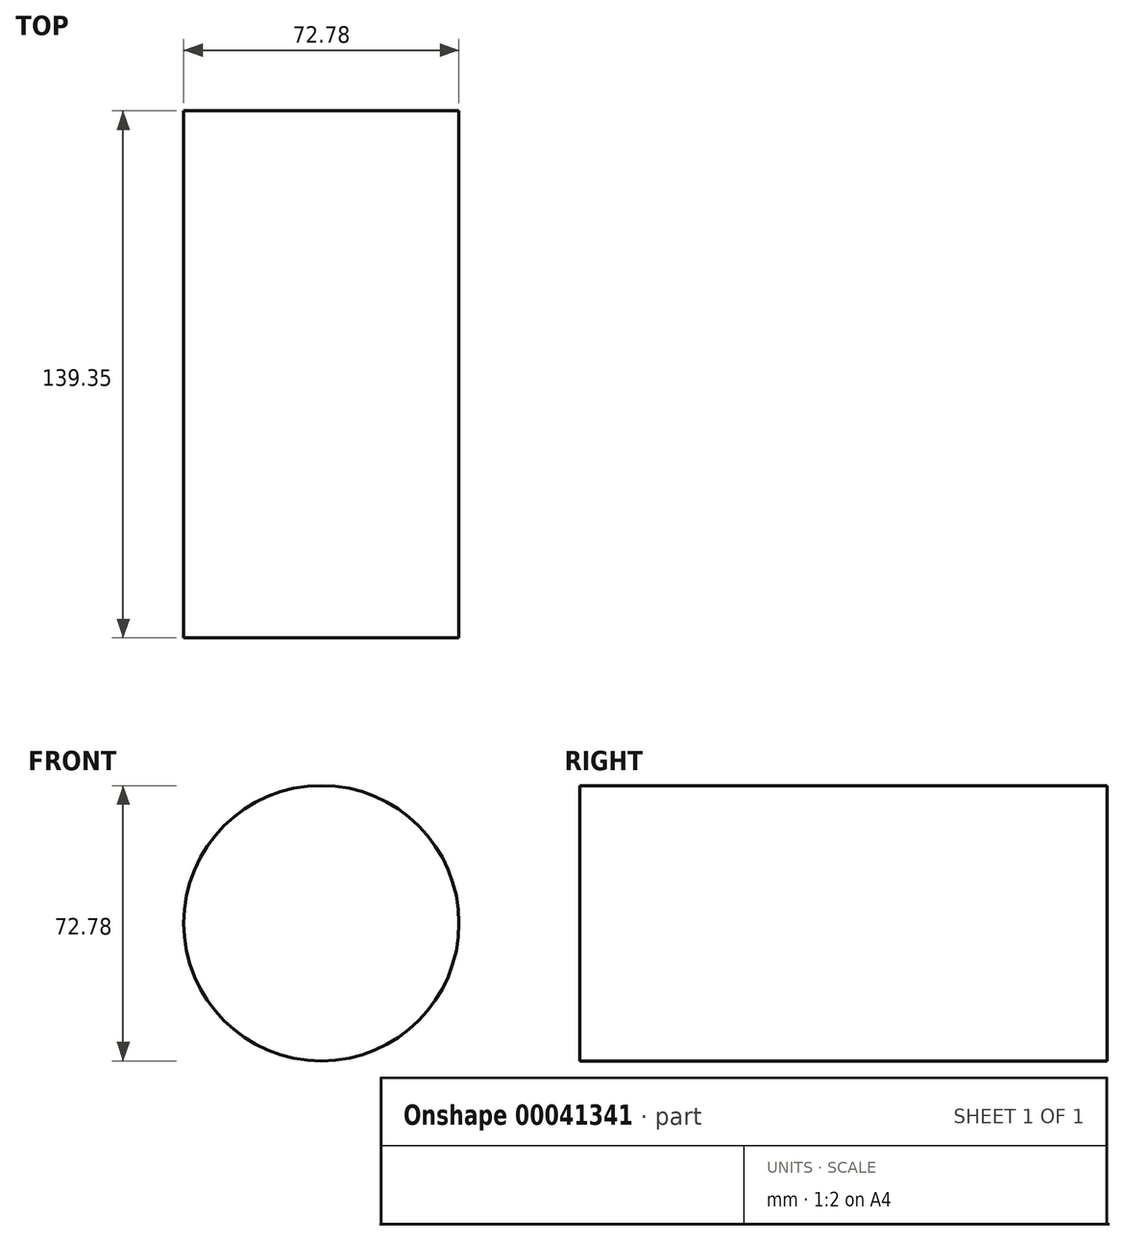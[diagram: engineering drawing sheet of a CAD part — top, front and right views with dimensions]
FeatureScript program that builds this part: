
annotation { "Feature Type Name" : "Feature", "Feature Type Description" : "" }
export const myFeature = defineFeature(function(context is Context, id is Id, definition is map)
    precondition{}
    {
        {
            var Q0;
            Q0=qCreatedBy(makeId("Front.planeOp"),FACE);
            var sketch = newSketch(context, id + "F0", { "sketchPlane" : qUnion([Q0])});
            skCircle(sketch, "E0", {"center": v(0, 0) * mm, "radius": 36.39 * mm});
            skSolve(sketch);
        }
        {
            var Q0;
            Q0=makeQuery(id+"F0.imprint","IMPRINT",FACE,{"disambiguationData":[TD([[makeQuery(id+"F0.imprint","IMPRINT",EDGE,{"derivedFrom":sQuery(id+"F0.wireOp",EDGE,"E0")}),1.0]])]});
            extrude(context, id + "F1", {"entities" : qUnion([Q0]), "depth" : 139.35 * mm});
        }
    });
